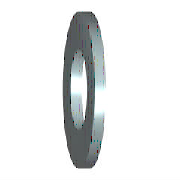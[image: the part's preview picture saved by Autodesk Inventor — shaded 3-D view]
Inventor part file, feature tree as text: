
AUTODESK INVENTOR PART (.ipt)
format: ipt  version: 2015 (Build 190159000, 159)  size: 120,320 bytes
history: native  units: mm (DEFAULTED — no unit token found)
features: extrude x1, other x1, plane x1, sketch x1
ambient origin geometry x7: Origin, YZ Plane, XY Plane, X Axis, Y Axis, Z Axis, Center Point
bodies: Solid1 (feature_tree)
feature tree (4):
  extrude  "Bryła"  Depth=13.0mm
  other  "Work Axis1"
  plane  "Work Plane1"
  sketch  "Szkic"
